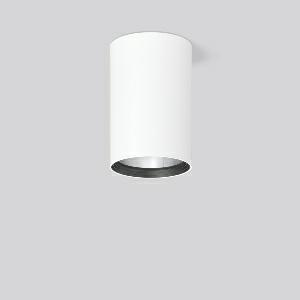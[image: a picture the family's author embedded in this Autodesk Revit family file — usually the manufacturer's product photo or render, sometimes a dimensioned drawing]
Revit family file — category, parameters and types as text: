
# Revit family: heledon_maxi_a_931223_002_1_917e
name_source: partatom
category: Lighting Fixtures
units: mm (PartAtom-declared; Revit-internal decimal feet)

## family parameters
Cut with Voids When Loaded = No
Host = Face
Light Source = No
Part Type = Normal
Room Calculation Point = No
Round Connector Dimension = Use Diameter
Shared = No

## types (1)
- HELEDON maxi A (1 x LED Modul 940, 4400 lm, 4000)
    Apparent Load = 35 VA
    Approval mark = CE
    CIE Flux Codes = 100 100 100 100 100
    Color Rendering = 92
    Color Temperature = 4000
    Default Elevation = 1800 mm
    Description = Series: HELEDON maxi
Cylindrical surface-mounted downlight. Housing: die-cast aluminium, powder-coated. Internal ceiling frame polycarbonate with bayonet mounting. Black plastic ring and recessed LED to prevent glare from the side. Optical assembly with reflector made of MIRO-Silver with 98% total light reflection for outstanding efficiency - can be changed without tools. Best colour rendering index Ra>90. Suitable for Ceiling mounting. Easy installation with a separate ceiling frame with bayonet mounting and plug connection. Driver integrated. Connected via plug-in connector. High quality converter without flickering and stroboscopic effect. The following accessories can be mounted without use of tools: interchangeable lenses, decorative glasses, honeycomb louvre, clear and frosted diffusers, white interchangeable plastic ring. 
Colour: traffic white, matt (RAL 9016)
Diameter: 123 mm
Height: 183 mm
Lamp: LED
Socket: without socket
Colour temperature: 4000K
Colour rendering index (CRI): 92
System power: 35 W
Rated luminous flux: 4400 lm
Luminous efficiency: 126 lm/W
Control gear: Regulated power supply
Protection class: I
Type of protection: IP 20
    Height = 183 mm
    Lamp = 1 x LED Modul 940
    Lamp Light Flux = 4400 lm
    Lamp count = 1
    Length = 123 mm
    Lifetime = 50000 h
    Luminous efficacy = 126 lm/W
    Manufacturer = RZB
    ModVariant = No
    Model = 931223.002.1
    Mounting Place = Ceiling
    Mounting Type = Surface mounted
    Number of Poles = 1
    OnlyDefault = Yes
    Power Factor = 1
    Product Name = HELEDON maxi A
    Product group = Surface mounted downlights
    ProductGroupID = 302
    Protection Class = Protection class I
    Protection Degree = IP 20
    RLX_Detail_Level = 1
    RLX_Emergency_Light_Flux = 0 lm
    RLX_Emergency_Type = 0
    RLX_Emergency_Type_DB = No
    RlxData = <blob elided: 97017 chars, md5=89ef3552>
    Socket = socket
    Standby Power = 0 W
    System Light Flux = 4400 lm
    System Power = 35 W
    Type Comments = Product without accessories
    Type Image = 931192.002.jpg
    URL = http://relux.com
    VarID = ---
    Voltage = 230 V
    Voltage Range = 220-240 V
    Weight = 0.00 kg
    Width = 0 mm  [stored 0 ft]

note: [stored X ft] marks values corroborated as IEEE doubles in the binary element streams (Revit-internal decimal feet)

## geometry (parser evidence)
native form markers: Blend x4, Sweep x12
no freeform markers — native parametric forms only
